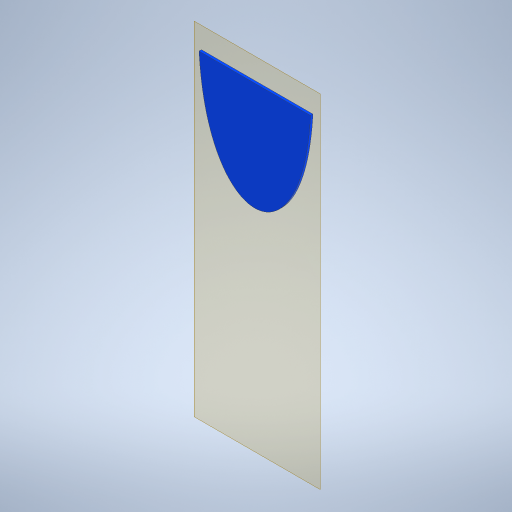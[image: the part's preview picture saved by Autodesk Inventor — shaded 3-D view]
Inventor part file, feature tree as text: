
AUTODESK INVENTOR PART (.ipt)
format: ipt  version: 2023 (Build 270158030, 158C)  size: 249,344 bytes
history: native  units: mm
features: other x3, plane x1, extrude x1, sketch x1, reference x1
ambient origin geometry x8: Origin, YZ Plane, XZ Plane, XY Plane, X Axis, Y Axis, Z Axis, Center Point
bodies: Solid1 (feature_tree)
feature tree (7):
  plane  "Work Plane1"
  extrude  "Extrusion1"  Depth=900.0mm
  sketch  "Sketch1"  dims[d0=700.0mm d1=900.0mm d2=350.0mm d3=350.0mm d4=40.0mm d5=40.0mm d6=15.0mm d7=0.0mm d8=10.0mm]
  reference  "Reference1"
  other  "<userpath>\Documents\0004-inventor\3D-CAD-main\primary-engineer-bench.iam"
  other  "primary-engineer-bench.iam"
  other  "bed-base:1"
